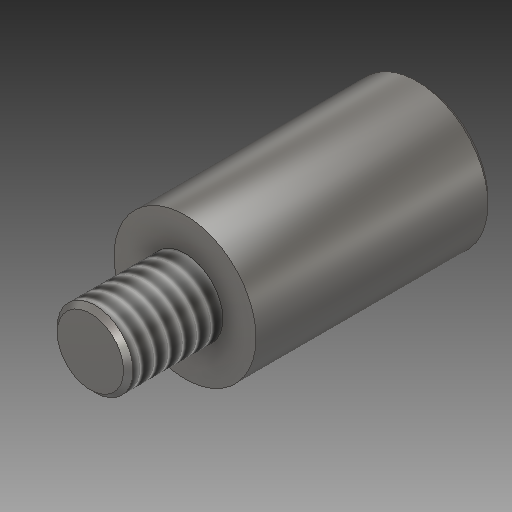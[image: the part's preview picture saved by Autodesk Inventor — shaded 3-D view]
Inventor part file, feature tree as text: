
AUTODESK INVENTOR PART (.ipt)
format: ipt  version: 2018 (Build 220112000, 112)  size: 151,552 bytes
history: native  units: mm
features: extrude x2, sketch x2, chamfer x1, thread x1
ambient origin geometry x8: Origin, YZ Plane, XZ Plane, XY Plane, X Axis, Y Axis, Z Axis, Center Point
bodies: Solido1 (feature_tree)
feature tree (6):
  extrude  "Estrusione1"  Depth=15.0mm
  extrude  "Estrusione2"  Depth=25.0mm TaperAngle=0.0deg
  chamfer  "Smusso1"  Distance=8.0mm
  thread  "Filettatura2"
  sketch  "Schizzo1"
  sketch  "Schizzo2"
